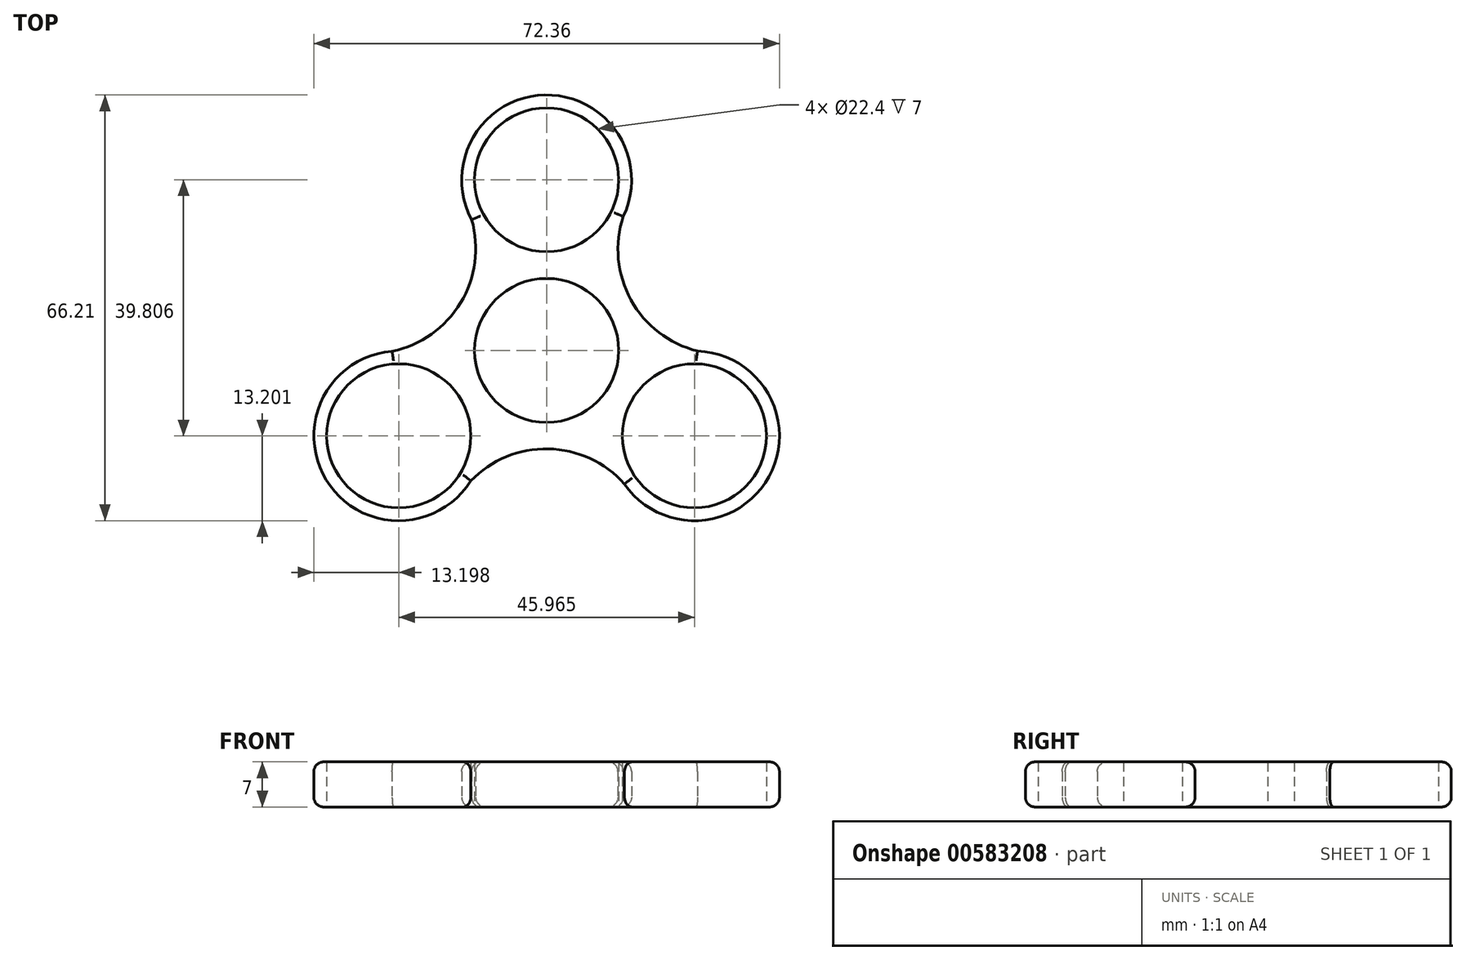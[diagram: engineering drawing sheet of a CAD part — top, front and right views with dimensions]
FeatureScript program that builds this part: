
annotation { "Feature Type Name" : "Feature", "Feature Type Description" : "" }
export const myFeature = defineFeature(function(context is Context, id is Id, definition is map)
    precondition{}
    {
        {
            var Q0;
            Q0=qCreatedBy(makeId("Top.planeOp"),FACE);
            var sketch = newSketch(context, id + "F0", { "sketchPlane" : qUnion([Q0])});
            skCircle(sketch, "E0", {"center": v(0, 0) * mm, "radius": 11.2 * mm});
            skCircle(sketch, "E1", {"center": v(0, 26.54) * mm, "radius": 11.2 * mm});
            skArc(sketch, "E2", {"start": v(11.91, 20.86) * mm, "mid": v(-0.29, 39.73) * mm, "end": v(-11.66, 20.34) * mm});
            skArc(sketch, "E3.1.0", {"start": v(-24.02, -0.1) * mm, "mid": v(-34.27, -20.12) * mm, "end": v(-11.79, -20.27) * mm});
            skCircle(sketch, "E3.1.1", {"center": v(-22.98, -13.27) * mm, "radius": 11.2 * mm});
            skArc(sketch, "E3.2.0", {"start": v(12.1, -20.75) * mm, "mid": v(34.55, -19.62) * mm, "end": v(23.45, -0.08) * mm});
            skCircle(sketch, "E3.2.1", {"center": v(22.98, -13.27) * mm, "radius": 11.2 * mm});
            skArc(sketch, "E4", {"start": v(11.91, 20.86) * mm, "mid": v(13.11, 7.87) * mm, "end": v(23.45, -0.08) * mm});
            skArc(sketch, "E5.1.0", {"start": v(-24.02, -0.1) * mm, "mid": v(-13.37, 7.42) * mm, "end": v(-11.66, 20.34) * mm});
            skArc(sketch, "E5.2.0", {"start": v(12.1, -20.75) * mm, "mid": v(0.26, -15.3) * mm, "end": v(-11.79, -20.27) * mm});
            skSolve(sketch);
        }
        {
            var Q0;
            Q0=makeQuery(id+"F0.imprint","IMPRINT",FACE,{"disambiguationData":[TD([[makeQuery(id+"F0.imprint","IMPRINT",EDGE,{"derivedFrom":sQuery(id+"F0.wireOp",EDGE,"E0")}),-1.0]])]});
            extrude(context, id + "F1", {"entities" : qUnion([Q0]), "depth" : 7 * mm, "offsetDistance" : 25 * mm});
        }
        {
            var Q0;
            Q0=makeQuery(id+"F1.opExtrude","CAP_EDGE",EDGE,{"disambiguationData":[OSD([sQuery(id+"F0.wireOp",EDGE,"E5.2.0")])],"isStart":false});
            var Q1;
            Q1=makeQuery(id+"F1.opExtrude","CAP_EDGE",EDGE,{"disambiguationData":[OSD([sQuery(id+"F0.wireOp",EDGE,"E3.2.0")])],"isStart":false});
            var Q2;
            Q2=makeQuery(id+"F1.opExtrude","CAP_EDGE",EDGE,{"disambiguationData":[OSD([sQuery(id+"F0.wireOp",EDGE,"E3.1.0")])],"isStart":false});
            var Q3;
            Q3=makeQuery(id+"F1.opExtrude","CAP_EDGE",EDGE,{"disambiguationData":[OSD([sQuery(id+"F0.wireOp",EDGE,"E5.1.0")])],"isStart":false});
            var Q4;
            Q4=makeQuery(id+"F1.opExtrude","CAP_EDGE",EDGE,{"disambiguationData":[OSD([sQuery(id+"F0.wireOp",EDGE,"E4")])],"isStart":false});
            var Q5;
            Q5=makeQuery(id+"F1.opExtrude","CAP_EDGE",EDGE,{"disambiguationData":[OSD([sQuery(id+"F0.wireOp",EDGE,"E2")])],"isStart":false});
            fillet(context, id + "F2", {"entities" : qUnion([Q0, Q1, Q2, Q3, Q4, Q5]), "radius" : 1.5 * mm, "tangentPropagation" : true, "allowEdgeOverflow" : false});
        }
        {
            var Q0;
            Q0=makeQuery(id+"F1.opExtrude","CAP_EDGE",EDGE,{"disambiguationData":[OSD([sQuery(id+"F0.wireOp",EDGE,"E5.2.0")])],"isStart":true});
            var Q1;
            Q1=makeQuery(id+"F1.opExtrude","CAP_EDGE",EDGE,{"disambiguationData":[OSD([sQuery(id+"F0.wireOp",EDGE,"E3.2.0")])],"isStart":true});
            var Q2;
            Q2=makeQuery(id+"F1.opExtrude","CAP_EDGE",EDGE,{"disambiguationData":[OSD([sQuery(id+"F0.wireOp",EDGE,"E4")])],"isStart":true});
            var Q3;
            Q3=makeQuery(id+"F1.opExtrude","CAP_EDGE",EDGE,{"disambiguationData":[OSD([sQuery(id+"F0.wireOp",EDGE,"E2")])],"isStart":true});
            var Q4;
            Q4=makeQuery(id+"F1.opExtrude","CAP_EDGE",EDGE,{"disambiguationData":[OSD([sQuery(id+"F0.wireOp",EDGE,"E5.1.0")])],"isStart":true});
            var Q5;
            Q5=makeQuery(id+"F1.opExtrude","CAP_EDGE",EDGE,{"disambiguationData":[OSD([sQuery(id+"F0.wireOp",EDGE,"E3.1.0")])],"isStart":true});
            fillet(context, id + "F3", {"entities" : qUnion([Q0, Q1, Q2, Q3, Q4, Q5]), "radius" : 1.5 * mm, "tangentPropagation" : true, "allowEdgeOverflow" : false});
        }
    });
